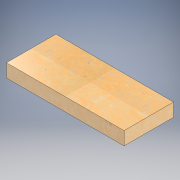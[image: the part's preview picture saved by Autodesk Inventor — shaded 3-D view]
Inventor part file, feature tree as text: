
AUTODESK INVENTOR PART (.ipt)
format: ipt  version: 2022.2 (Build 262287010, 287A)  size: 132,608 bytes
history: native  units: in
note: dims shown in document units (in); Inventor stores cm internally (conversion verified against a paired STEP export)
features: extrude x1, sketch x1
ambient origin geometry x8: Origin, YZ Plane, XZ Plane, XY Plane, X Axis, Y Axis, Z Axis, Center Point
bodies: Solid1 (feature_tree)
feature tree (2):
  extrude  "Extrusion1"  Depth=15.0in
  sketch  "Sketch1"  dims[d0=35.625in d1=15.0in d2=4.0in d3=0.0in]
